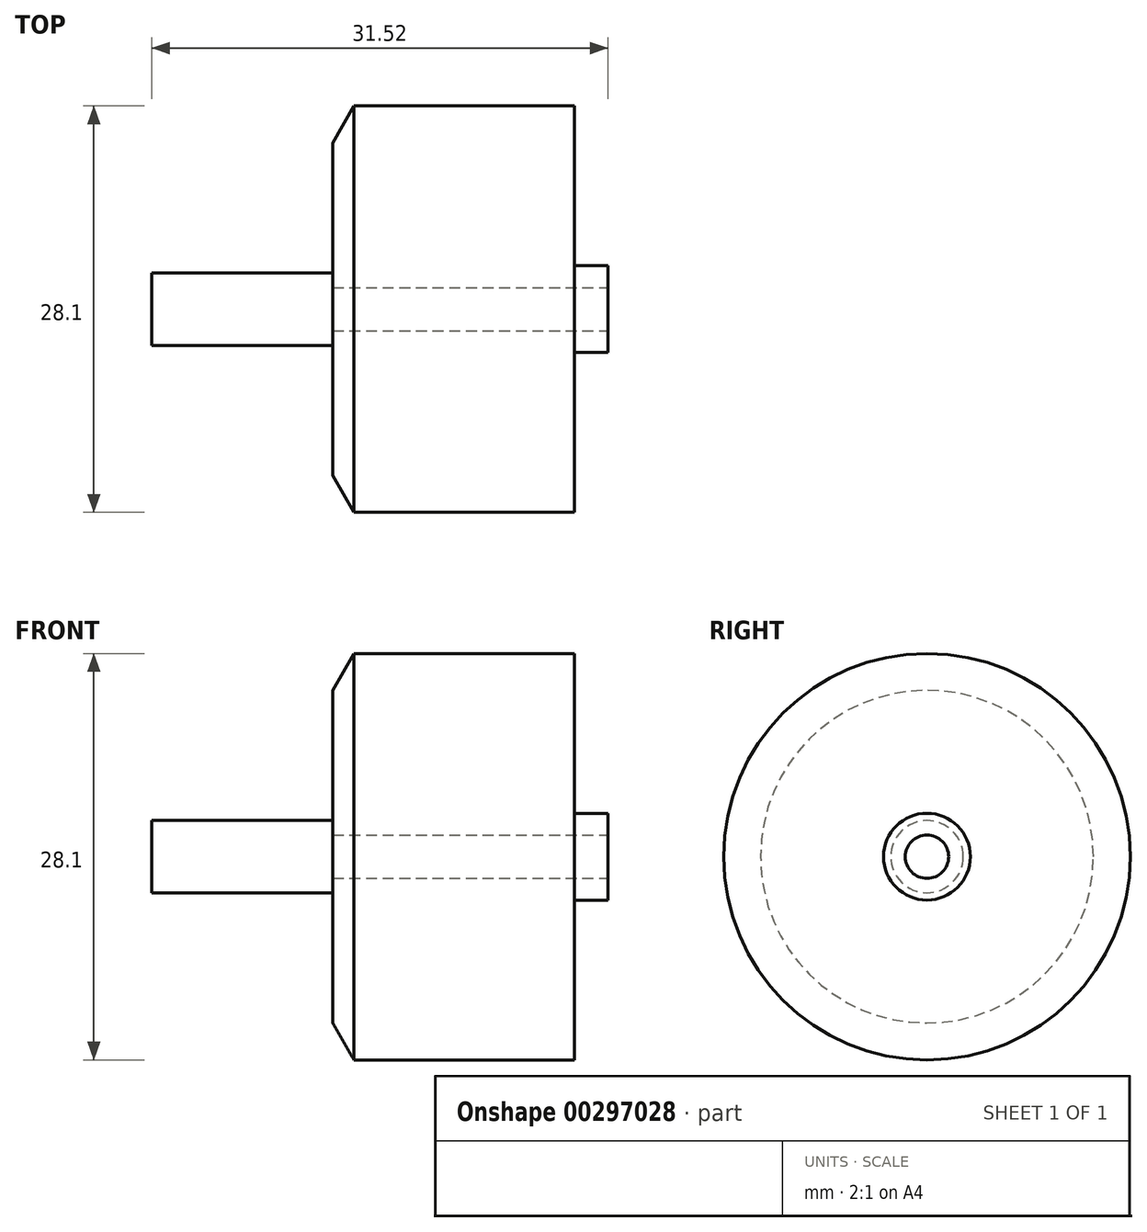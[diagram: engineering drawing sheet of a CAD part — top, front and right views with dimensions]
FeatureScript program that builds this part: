
annotation { "Feature Type Name" : "Feature", "Feature Type Description" : "" }
export const myFeature = defineFeature(function(context is Context, id is Id, definition is map)
    precondition{}
    {
        {
            var Q0;
            Q0=qCreatedBy(makeId("Front.planeOp"),FACE);
            var sketch = newSketch(context, id + "F0", { "sketchPlane" : qUnion([Q0])});
            skLineSegment(sketch, "E0.bottom", {"start": v(-16.7, 14.05) * mm, "end": v(0, 14.05) * mm});
            skLineSegment(sketch, "E0.top", {"start": v(-16.7, -14.05) * mm, "end": v(0, -14.05) * mm});
            skLineSegment(sketch, "E0.left", {"start": v(-16.7, 14.05) * mm, "end": v(-16.7, -14.05) * mm});
            skLineSegment(sketch, "E0.right", {"start": v(0, 14.05) * mm, "end": v(0, -14.05) * mm});
            skLineSegment(sketch, "E1.bottom", {"start": v(-16.71, -11.5) * mm, "end": v(-16.7, -11.5) * mm});
            skLineSegment(sketch, "E1.top", {"start": v(-16.71, 11.5) * mm, "end": v(-16.7, 11.5) * mm});
            skLineSegment(sketch, "E1.left", {"start": v(-16.71, 11.5) * mm, "end": v(-16.71, -11.5) * mm});
            skLineSegment(sketch, "E1.right", {"start": v(-16.7, 11.5) * mm, "end": v(-16.7, -11.5) * mm});
            skLineSegment(sketch, "E2", {"start": v(2.3, 0) * mm, "end": v(-29.21, 0) * mm});
            skLineSegment(sketch, "E3.bottom", {"start": v(-16.7, 1.5) * mm, "end": v(2.3, 1.5) * mm});
            skLineSegment(sketch, "E3.top", {"start": v(-16.7, -1.5) * mm, "end": v(2.3, -1.5) * mm});
            skLineSegment(sketch, "E3.left", {"start": v(-16.7, 1.5) * mm, "end": v(-16.7, -1.5) * mm});
            skLineSegment(sketch, "E3.right", {"start": v(2.3, 1.5) * mm, "end": v(2.3, -1.5) * mm});
            skPoint(sketch, "E4", {"position": v(2.3, 0) * mm});
            skPoint(sketch, "E5", {"position": v(-16.71, 0) * mm});
            skLineSegment(sketch, "E6.bottom", {"start": v(-29.2, 2.5) * mm, "end": v(-16.71, 2.5) * mm});
            skLineSegment(sketch, "E6.top", {"start": v(-29.2, -2.5) * mm, "end": v(-16.71, -2.5) * mm});
            skLineSegment(sketch, "E6.left", {"start": v(-29.21, 2.5) * mm, "end": v(-29.21, -2.5) * mm});
            skLineSegment(sketch, "E6.right", {"start": v(-16.71, 2.5) * mm, "end": v(-16.71, -2.5) * mm});
            skLineSegment(sketch, "E7.bottom", {"start": v(0, 3) * mm, "end": v(2.3, 3) * mm});
            skLineSegment(sketch, "E7.top", {"start": v(0, -3) * mm, "end": v(2.3, -3) * mm});
            skLineSegment(sketch, "E7.left", {"start": v(0, 3) * mm, "end": v(0, -3) * mm});
            skLineSegment(sketch, "E7.right", {"start": v(2.31, 3) * mm, "end": v(2.3, -3) * mm});
            skLineSegment(sketch, "E8", {"start": v(0, 11.5) * mm, "end": v(0, -11.5) * mm});
            skPoint(sketch, "E9", {"position": v(0, 0) * mm});
            skLineSegment(sketch, "E10", {"start": v(-16.7, 11.5) * mm, "end": v(-15.23, 14.05) * mm});
            skSolve(sketch);
        }
        {
            var Q0;
            Q0=qCreatedBy(makeId("Front.planeOp"),FACE);
            var sketch = newSketch(context, id + "F1", { "sketchPlane" : qUnion([Q0])});
            skLineSegment(sketch, "E11.0", {"start": v(-16.7, 14.05) * mm, "end": v(0, 14.05) * mm});
            skLineSegment(sketch, "E11.1", {"start": v(-16.7, 14.05) * mm, "end": v(-16.7, -14.05) * mm});
            skLineSegment(sketch, "E11.2", {"start": v(0, 14.05) * mm, "end": v(0, -14.05) * mm});
            skLineSegment(sketch, "E11.3", {"start": v(-16.7, -14.05) * mm, "end": v(0, -14.05) * mm});
            skLineSegment(sketch, "E11.4", {"start": v(2.3, 0) * mm, "end": v(-29.21, 0) * mm});
            skLineSegment(sketch, "E12.0", {"start": v(0, 3) * mm, "end": v(2.3, 3) * mm});
            skLineSegment(sketch, "E12.1", {"start": v(0, -3) * mm, "end": v(2.3, -3) * mm});
            skLineSegment(sketch, "E12.2", {"start": v(2.31, 3) * mm, "end": v(2.3, -3) * mm});
            skLineSegment(sketch, "E13.0", {"start": v(-16.7, 1.5) * mm, "end": v(2.3, 1.5) * mm});
            skLineSegment(sketch, "E14.0", {"start": v(-16.7, 11.5) * mm, "end": v(-15.23, 14.05) * mm});
            skSolve(sketch);
        }
        {
            var Q0;
            Q0=qCreatedBy(makeId("Front.planeOp"),FACE);
            var sketch = newSketch(context, id + "F2", { "sketchPlane" : qUnion([Q0])});
            skLineSegment(sketch, "E15.0", {"start": v(-16.7, 1.5) * mm, "end": v(-16.7, -1.5) * mm});
            skLineSegment(sketch, "E15.1", {"start": v(-16.7, 1.5) * mm, "end": v(2.3, 1.5) * mm});
            skLineSegment(sketch, "E15.2", {"start": v(2.3, 0) * mm, "end": v(-29.21, 0) * mm});
            skLineSegment(sketch, "E15.3", {"start": v(-16.7, -1.5) * mm, "end": v(2.3, -1.5) * mm});
            skLineSegment(sketch, "E15.4", {"start": v(2.3, 1.5) * mm, "end": v(2.3, -1.5) * mm});
            skSolve(sketch);
        }
        {
            var Q0;
            Q0=qCreatedBy(makeId("Front.planeOp"),FACE);
            var sketch = newSketch(context, id + "F3", { "sketchPlane" : qUnion([Q0])});
            skLineSegment(sketch, "E16.0", {"start": v(-16.71, 11.5) * mm, "end": v(-16.71, -11.5) * mm});
            skLineSegment(sketch, "E16.1", {"start": v(-29.2, -2.5) * mm, "end": v(-16.71, -2.5) * mm});
            skLineSegment(sketch, "E16.2", {"start": v(-29.21, 2.5) * mm, "end": v(-29.21, -2.5) * mm});
            skLineSegment(sketch, "E16.3", {"start": v(-29.2, 2.5) * mm, "end": v(-16.71, 2.5) * mm});
            skLineSegment(sketch, "E16.4", {"start": v(2.3, 0) * mm, "end": v(-29.21, 0) * mm});
            skLineSegment(sketch, "E16.5", {"start": v(-16.71, -11.5) * mm, "end": v(-16.7, -11.5) * mm});
            skLineSegment(sketch, "E16.6", {"start": v(-16.71, 11.5) * mm, "end": v(-16.7, 11.5) * mm});
            skLineSegment(sketch, "E16.7", {"start": v(-16.7, 11.5) * mm, "end": v(-16.7, -11.5) * mm});
            skSolve(sketch);
        }
        {
            var Q0;
            {var subQ0=sQuery(id+"F1.wireOp",EDGE,"E12.0");Q0=makeQuery(id+"F1.imprint","IMPRINT",FACE,{"disambiguationData":[TD([[makeQuery(id+"F1.imprint","IMPRINT",EDGE,{"derivedFrom":subQ0}),-1.0]])]});}
            var Q1;
            {var subQ4=sQuery(id+"F1.wireOp",EDGE,"E14.0");Q1=makeQuery(id+"F1.imprint","IMPRINT",FACE,{"disambiguationData":[TD([[makeQuery(id+"F1.imprint","IMPRINT",EDGE,{"derivedFrom":subQ4}),-1.0]])]});}
            var Q2;
            Q2=sQuery(id+"F1.wireOp",EDGE,"E11.4");
            revolve(context, id + "F4", {"surfaceOperationType" : NewSurfaceOperationType.NEW, "entities" : qUnion([Q0, Q1]), "axis" : qUnion([Q2]), "revolveType" : RevolveType.FULL});
        }
        {
            var Q0;
            {var subQ0=sQuery(id+"F2.wireOp",EDGE,"E15.1");Q0=makeQuery(id+"F2.imprint","IMPRINT",FACE,{"disambiguationData":[TD([[makeQuery(id+"F2.imprint","IMPRINT",EDGE,{"derivedFrom":subQ0}),-1.0]])]});}
            var Q1;
            Q1=sQuery(id+"F2.wireOp",EDGE,"E15.2");
            revolve(context, id + "F5", {"surfaceOperationType" : NewSurfaceOperationType.NEW, "entities" : qUnion([Q0]), "axis" : qUnion([Q1]), "revolveType" : RevolveType.FULL});
        }
        {
            var Q0;
            {var subQ0=sQuery(id+"F3.wireOp",EDGE,"E16.3");Q0=makeQuery(id+"F3.imprint","IMPRINT",FACE,{"disambiguationData":[TD([[makeQuery(id+"F3.imprint","IMPRINT",EDGE,{"derivedFrom":subQ0}),-1.0]])]});}
            var Q1;
            {var subQ5=sQuery(id+"F3.wireOp",EDGE,"E16.6");Q1=makeQuery(id+"F3.imprint","IMPRINT",FACE,{"disambiguationData":[TD([[makeQuery(id+"F3.imprint","IMPRINT",EDGE,{"derivedFrom":subQ5}),-1.0]])]});}
            var Q2;
            Q2=sQuery(id+"F3.wireOp",EDGE,"E16.4");
            revolve(context, id + "F6", {"surfaceOperationType" : NewSurfaceOperationType.NEW, "entities" : qUnion([Q0, Q1]), "axis" : qUnion([Q2]), "revolveType" : RevolveType.FULL});
        }
    });
